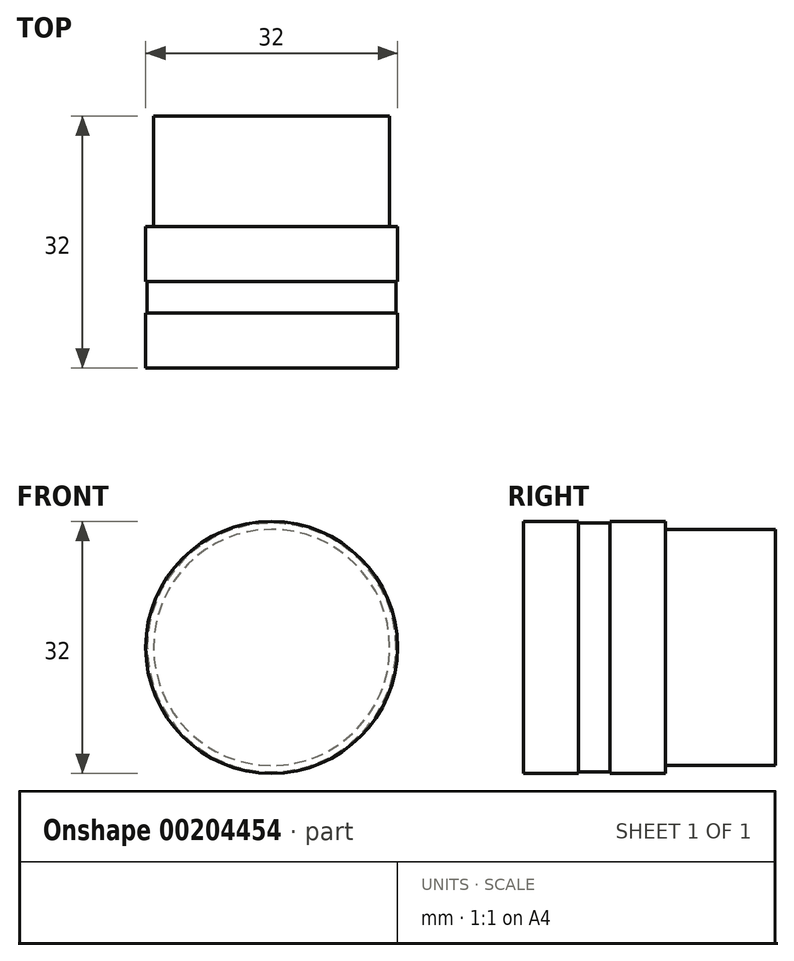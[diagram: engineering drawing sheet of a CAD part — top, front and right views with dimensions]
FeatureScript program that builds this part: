
annotation { "Feature Type Name" : "Feature", "Feature Type Description" : "" }
export const myFeature = defineFeature(function(context is Context, id is Id, definition is map)
    precondition{}
    {
        {
            var Q0;
            Q0=qCreatedBy(makeId("Right.planeOp"),FACE);
            var sketch = newSketch(context, id + "F0", { "sketchPlane" : qUnion([Q0])});
            skLineSegment(sketch, "E0", {"start": v(0, 0) * mm, "end": v(0, 16) * mm});
            skLineSegment(sketch, "E1", {"start": v(0, 16) * mm, "end": v(7, 16) * mm});
            skLineSegment(sketch, "E2", {"start": v(7, 16) * mm, "end": v(7, 15.8) * mm});
            skLineSegment(sketch, "E3", {"start": v(7, 15.8) * mm, "end": v(11, 15.8) * mm});
            skLineSegment(sketch, "E4", {"start": v(11, 15.8) * mm, "end": v(11, 16) * mm});
            skLineSegment(sketch, "E5", {"start": v(11, 16) * mm, "end": v(18, 16) * mm});
            skLineSegment(sketch, "E6", {"start": v(18, 16) * mm, "end": v(18, 15) * mm});
            skLineSegment(sketch, "E7", {"start": v(18, 15) * mm, "end": v(32, 15) * mm});
            skLineSegment(sketch, "E8", {"start": v(32, 15) * mm, "end": v(32, 0) * mm});
            skLineSegment(sketch, "E9", {"start": v(0, 0) * mm, "end": v(32, 0) * mm});
            skSolve(sketch);
        }
        {
            var Q0;
            Q0 = qSketchRegion(id + "F0", true);
            var Q1;
            Q1=sQuery(id+"F0.wireOp",EDGE,"E9");
            revolve(context, id + "F1", {"entities" : qUnion([Q0]), "axis" : qUnion([Q1]), "revolveType" : RevolveType.FULL});
        }
    });
